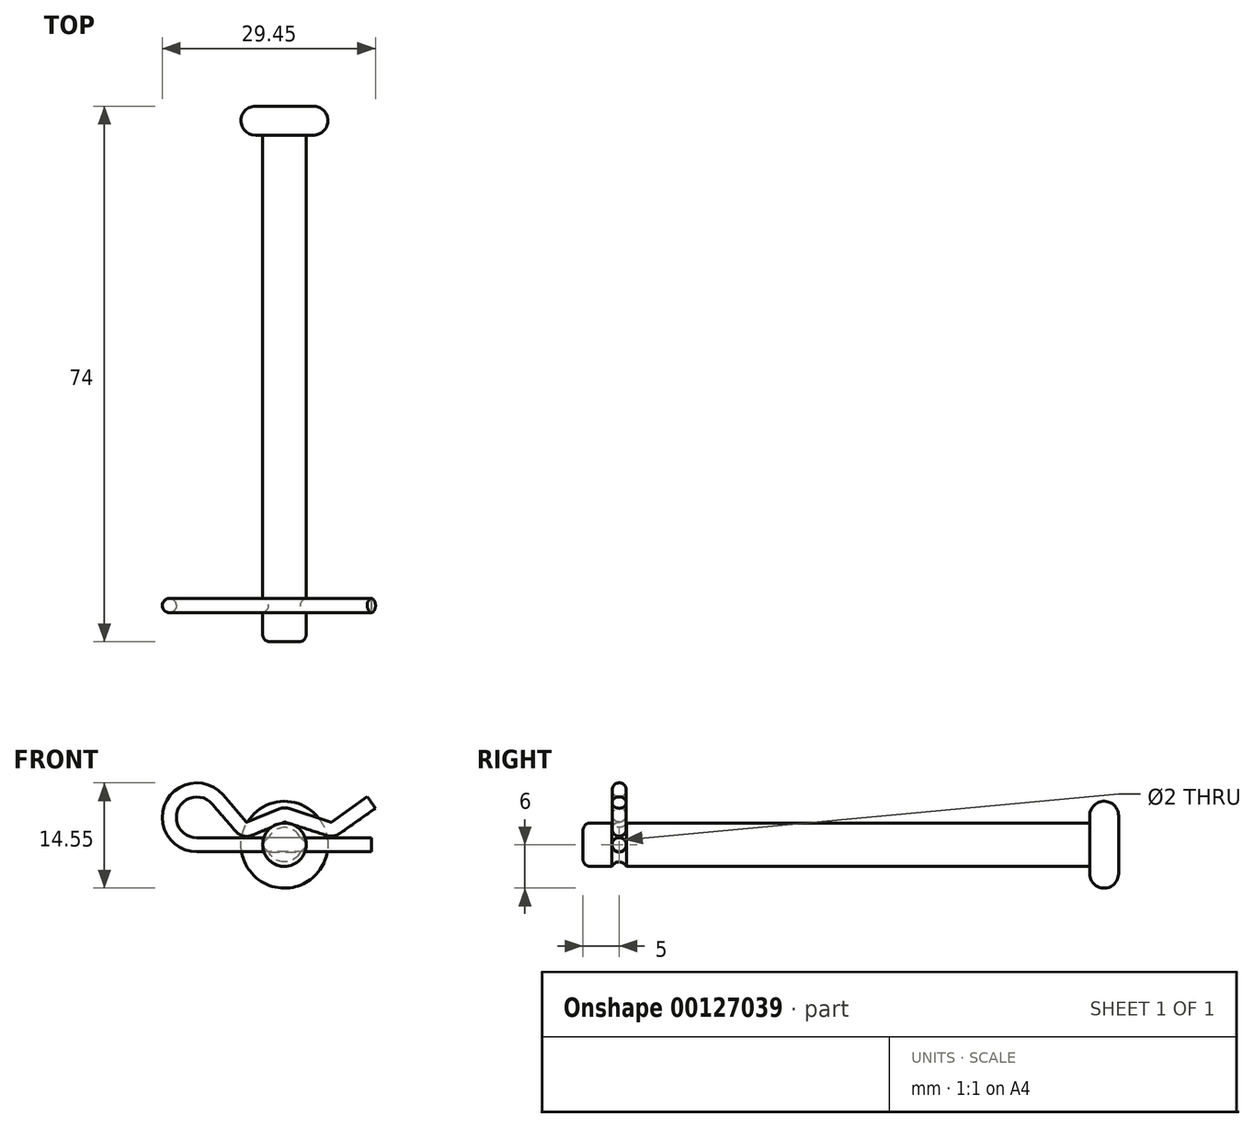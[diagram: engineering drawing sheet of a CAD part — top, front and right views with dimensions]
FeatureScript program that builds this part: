
annotation { "Feature Type Name" : "Feature", "Feature Type Description" : "" }
export const myFeature = defineFeature(function(context is Context, id is Id, definition is map)
    precondition{}
    {
        {
            var Q0;
            Q0=qCreatedBy(makeId("Front.planeOp"),FACE);
            var sketch = newSketch(context, id + "F0", { "sketchPlane" : qUnion([Q0])});
            skCircle(sketch, "E0", {"center": v(0, 0) * mm, "radius": 3 * mm});
            skCircle(sketch, "E1", {"center": v(0, 0) * mm, "radius": 6 * mm});
            skSolve(sketch);
        }
        {
            var Q0;
            Q0=makeQuery(id+"F0.imprint","IMPRINT",FACE,{"disambiguationData":[TD([[makeQuery(id+"F0.imprint","IMPRINT",EDGE,{"derivedFrom":sQuery(id+"F0.wireOp",EDGE,"E0")}),1.0]])]});
            extrude(context, id + "F1", {"entities" : qUnion([Q0]), "depth" : 70 * mm});
        }
        {
            var Q0;
            Q0=makeQuery(id+"F0.imprint","IMPRINT",FACE,{"disambiguationData":[TD([[makeQuery(id+"F0.imprint","IMPRINT",EDGE,{"derivedFrom":sQuery(id+"F0.wireOp",EDGE,"E0")}),1.0]])]});
            var Q1;
            Q1=makeQuery(id+"F0.imprint","IMPRINT",FACE,{"disambiguationData":[TD([[makeQuery(id+"F0.imprint","IMPRINT",EDGE,{"derivedFrom":sQuery(id+"F0.wireOp",EDGE,"E0")}),-1.0]])]});
            extrude(context, id + "F2", {"entities" : qUnion([Q0, Q1]), "operationType" : NewBodyOperationType.ADD, "oppositeDirection" : true, "depth" : 4 * mm});
        }
        {
            var Q0;
            Q0=makeQuery(id+"F2.opExtrude","CAP_EDGE",EDGE,{"disambiguationData":[OSD([sQuery(id+"F0.wireOp",EDGE,"E1")])],"isStart":false});
            var Q1;
            Q1=makeQuery(id+"F2.opExtrude","CAP_EDGE",EDGE,{"disambiguationData":[OSD([sQuery(id+"F0.wireOp",EDGE,"E1")])],"isStart":true});
            fillet(context, id + "F3", {"entities" : qUnion([Q0, Q1]), "radius" : 2 * mm, "tangentPropagation" : true, "allowEdgeOverflow" : false});
        }
        {
            var Q0;
            Q0=makeQuery(id+"F1.opExtrude","CAP_EDGE",EDGE,{"disambiguationData":[OSD([sQuery(id+"F0.wireOp",EDGE,"E0")])],"isStart":false});
            fillet(context, id + "F4", {"entities" : qUnion([Q0]), "radius" : 1 * mm, "tangentPropagation" : true, "allowEdgeOverflow" : false});
        }
        {
            var Q0;
            Q0=qCreatedBy(makeId("Right.planeOp"),FACE);
            var sketch = newSketch(context, id + "F5", { "sketchPlane" : qUnion([Q0])});
            skLineSegment(sketch, "E2", {"start": v(0, 0) * mm, "end": v(-92.96, 0) * mm, "construction": true});
            skCircle(sketch, "E3", {"center": v(-65, 0) * mm, "radius": 1 * mm});
            skLineSegment(sketch, "E4.0", {"start": v(-70, -2) * mm, "end": v(-70, 2) * mm, "construction": true});
            skLineSegment(sketch, "E5", {"start": v(-65, 0) * mm, "end": v(-65, 3.5) * mm, "construction": true});
            skLineSegment(sketch, "E6", {"start": v(0, -3) * mm, "end": v(-69, -3) * mm});
            skLineSegment(sketch, "E7", {"start": v(-69, 3) * mm, "end": v(0, 3) * mm, "construction": true});
            skLineSegment(sketch, "E8", {"start": v(-63.88, 3.5) * mm, "end": v(-66.12, 3.5) * mm});
            skArc(sketch, "E9", {"start": v(-66.12, 3.5) * mm, "mid": v(-65, 2.38) * mm, "end": v(-63.88, 3.5) * mm});
            skLineSegment(sketch, "E10", {"start": v(-64, 3) * mm, "end": v(-66, 3) * mm});
            skSolve(sketch);
        }
        {
            var Q0;
            Q0=makeQuery(id+"F5.imprint","IMPRINT",FACE,{"disambiguationData":[TD([[makeQuery(id+"F5.imprint","IMPRINT",EDGE,{"derivedFrom":sQuery(id+"F5.wireOp",EDGE,"E3")}),1.0]])]});
            extrude(context, id + "F6", {"entities" : qUnion([Q0]), "operationType" : NewBodyOperationType.REMOVE, "endBound" : BoundingType.SYMMETRIC, "oppositeDirection" : true, "depth" : 6 * mm});
        }
        {
            var Q0;
            {var subQ0=sQuery(id+"F5.wireOp",EDGE,"E10");Q0=makeQuery(id+"F5.imprint","IMPRINT",FACE,{"disambiguationData":[TD([[makeQuery(id+"F5.imprint","IMPRINT",EDGE,{"derivedFrom":subQ0}),1.0]])]});}
            var Q1;
            Q1=sQuery(id+"F5.wireOp",EDGE,"E2");
            revolve(context, id + "F7", {"operationType" : NewBodyOperationType.REMOVE, "entities" : qUnion([Q0]), "axis" : qUnion([Q1]), "revolveType" : RevolveType.FULL, "oppositeDirection" : true});
        }
        {
            var Q0;
            Q0=sQuery(id+"F5.wireOp",VERTEX,"E3.center");
            var Q1;
            Q1=sQuery(id+"F5.wireOp",EDGE,"E2");
            cPlane(context, id + "F8", {"entities" : qUnion([Q0, Q1]), "cplaneType" : CPlaneType.LINE_POINT, "offset" : 25 * mm, "width" : 150 * mm, "height" : 150 * mm});
        }
        {
            var Q0;
            Q0=qCreatedBy(id+"F8.planeOp",FACE);
            var sketch = newSketch(context, id + "F9", { "sketchPlane" : qUnion([Q0])});
            skPoint(sketch, "E11.0", {"position": v(0, 0) * mm});
            skLineSegment(sketch, "E12.0", {"start": v(0, 1) * mm, "end": v(0, -1) * mm, "construction": true});
            skLineSegment(sketch, "E13", {"start": v(0, 0) * mm, "end": v(-18, 0) * mm, "construction": true});
            skLineSegment(sketch, "E14", {"start": v(0, 0) * mm, "end": v(24.02, 0) * mm, "construction": true});
            skArc(sketch, "E15", {"start": v(-9.24, 6.26) * mm, "mid": v(-15.56, 5.37) * mm, "end": v(-12.11, 0) * mm});
            skCircle(sketch, "E16.0", {"center": v(0, 0) * mm, "radius": 3 * mm, "construction": true});
            skLineSegment(sketch, "E17", {"start": v(0, 1) * mm, "end": v(0, 8.02) * mm, "construction": true});
            skLineSegment(sketch, "E18", {"start": v(-4.85, 2.2) * mm, "end": v(-0.34, 4.05) * mm});
            skLineSegment(sketch, "E19", {"start": v(0.35, 4.07) * mm, "end": v(6.16, 2.2) * mm});
            skLineSegment(sketch, "E20", {"start": v(7.05, 2.33) * mm, "end": v(12.01, 5.83) * mm});
            skLineSegment(sketch, "E21", {"start": v(-5.99, 2.47) * mm, "end": v(-9.24, 6.26) * mm});
            skLineSegment(sketch, "E22", {"start": v(12.01, 0) * mm, "end": v(-12.11, 0) * mm});
            skPoint(sketch, "E23.visualSharp", {"position": v(6.64, 2.05) * mm});
            skArc(sketch, "E23.filletArc", {"start": v(6.16, 2.2) * mm, "mid": v(6.62, 2.16) * mm, "end": v(7.05, 2.33) * mm});
            skLineSegment(sketch, "E24", {"start": v(12.01, 0) * mm, "end": v(12.01, 8.64) * mm, "construction": true});
            skPoint(sketch, "E25.visualSharp", {"position": v(-5.52, 1.93) * mm});
            skArc(sketch, "E25.filletArc", {"start": v(-5.99, 2.47) * mm, "mid": v(-5.46, 2.15) * mm, "end": v(-4.85, 2.2) * mm});
            skPoint(sketch, "E26.visualSharp", {"position": v(0, 4.19) * mm});
            skArc(sketch, "E26.filletArc", {"start": v(0.35, 4.07) * mm, "mid": v(0, 4.12) * mm, "end": v(-0.34, 4.05) * mm});
            skSolve(sketch);
        }
        {
            var Q0;
            Q0=sQuery(id+"F9.wireOp",VERTEX,"E24.start");
            var Q1;
            Q1=sQuery(id+"F9.wireOp",EDGE,"E22");
            cPlane(context, id + "F10", {"entities" : qUnion([Q0, Q1]), "cplaneType" : CPlaneType.LINE_POINT, "offset" : 25 * mm, "width" : 150 * mm, "height" : 150 * mm});
        }
        {
            var Q0;
            Q0=qCreatedBy(id+"F10.planeOp",FACE);
            var sketch = newSketch(context, id + "F11", { "sketchPlane" : qUnion([Q0])});
            skPoint(sketch, "E27.0", {"position": v(65, 0) * mm});
            skCircle(sketch, "E28", {"center": v(65, 0) * mm, "radius": 0.98 * mm});
            skSolve(sketch);
        }
        {
            var Q0;
            Q0=makeQuery(id+"F11.imprint","IMPRINT",FACE,{"disambiguationData":[TD([[makeQuery(id+"F11.imprint","IMPRINT",EDGE,{"derivedFrom":sQuery(id+"F11.wireOp",EDGE,"E28")}),1.0]])]});
            var Q1;
            Q1=sQuery(id+"F9.wireOp",EDGE,"E22");
            var Q2;
            Q2=sQuery(id+"F9.wireOp",EDGE,"E15");
            var Q3;
            Q3=sQuery(id+"F9.wireOp",EDGE,"E21");
            var Q4;
            Q4=sQuery(id+"F9.wireOp",EDGE,"E25.filletArc");
            var Q5;
            Q5=sQuery(id+"F9.wireOp",EDGE,"E18");
            var Q6;
            Q6=sQuery(id+"F9.wireOp",EDGE,"E26.filletArc");
            var Q7;
            Q7=sQuery(id+"F9.wireOp",EDGE,"E19");
            var Q8;
            Q8=sQuery(id+"F9.wireOp",EDGE,"E23.filletArc");
            var Q9;
            Q9=sQuery(id+"F9.wireOp",EDGE,"E20");
            sweep(context, id + "F12", {"profiles" : qUnion([Q0]), "path" : qUnion([Q1, Q2, Q3, Q4, Q5, Q6, Q7, Q8, Q9])});
        }
    });
